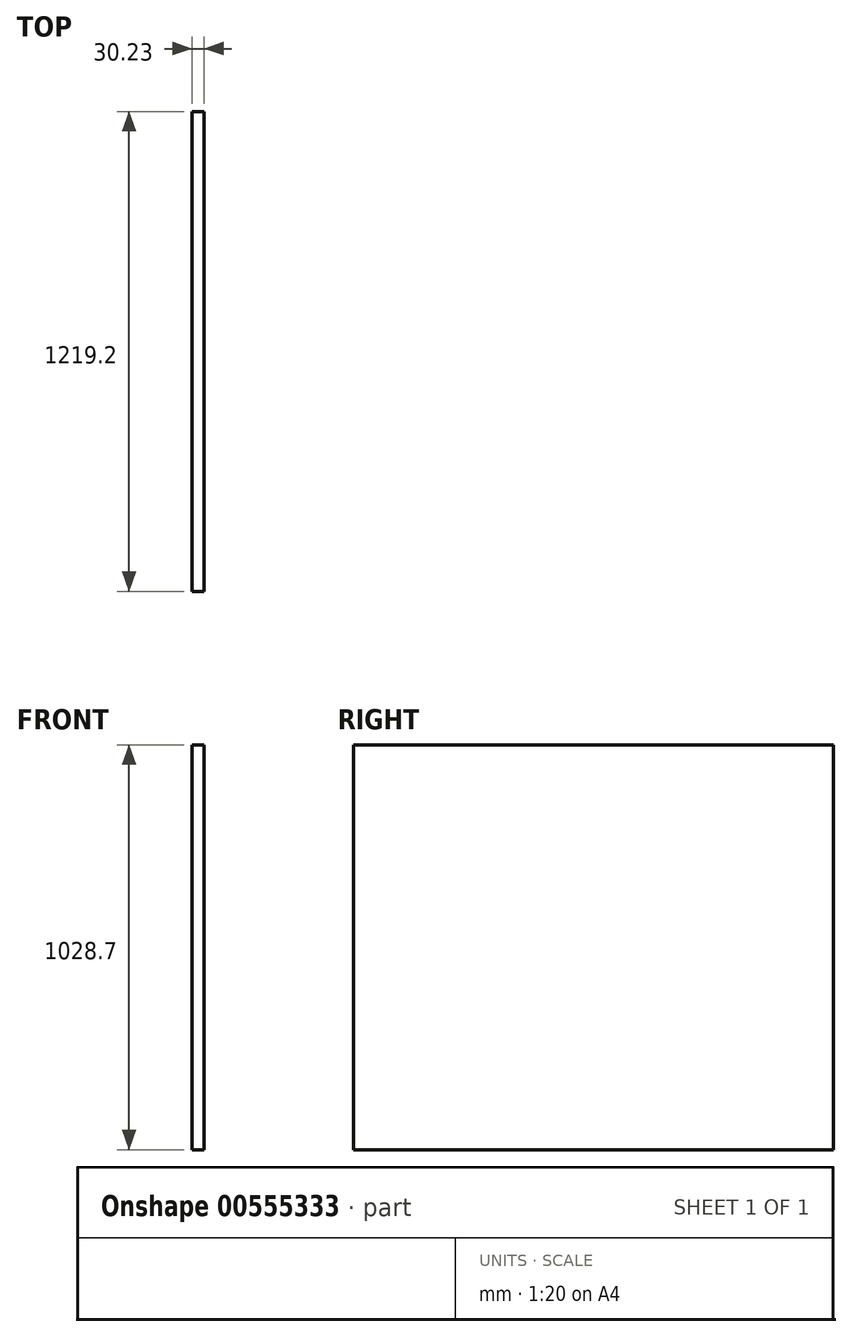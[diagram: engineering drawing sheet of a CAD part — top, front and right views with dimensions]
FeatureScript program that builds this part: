
annotation { "Feature Type Name" : "Feature", "Feature Type Description" : "" }
export const myFeature = defineFeature(function(context is Context, id is Id, definition is map)
    precondition{}
    {
        {
            var Q0;
            Q0=qCreatedBy(makeId("Right.planeOp"),FACE);
            var sketch = newSketch(context, id + "F0", { "sketchPlane" : qUnion([Q0])});
            skLineSegment(sketch, "E0.bottom", {"start": v(-609.6, 514.35) * mm, "end": v(609.6, 514.35) * mm});
            skLineSegment(sketch, "E0.top", {"start": v(-609.6, -514.35) * mm, "end": v(609.6, -514.35) * mm});
            skLineSegment(sketch, "E0.left", {"start": v(-609.6, 514.35) * mm, "end": v(-609.6, -514.35) * mm});
            skLineSegment(sketch, "E0.right", {"start": v(609.6, 514.35) * mm, "end": v(609.6, -514.35) * mm});
            skPoint(sketch, "E0.middle", {"position": v(0, 0) * mm});
            skSolve(sketch);
        }
        {
            var Q0;
            Q0=makeQuery(id+"F0.imprint","IMPRINT",FACE,{"disambiguationData":[TD([[makeQuery(id+"F0.imprint","IMPRINT",EDGE,{"derivedFrom":sQuery(id+"F0.wireOp",EDGE,"E0.bottom")}),-1.0]])]});
            extrude(context, id + "F1", {"entities" : qUnion([Q0]), "depth" : 30.23 * mm, "offsetDistance" : 25.4 * mm});
        }
    });
